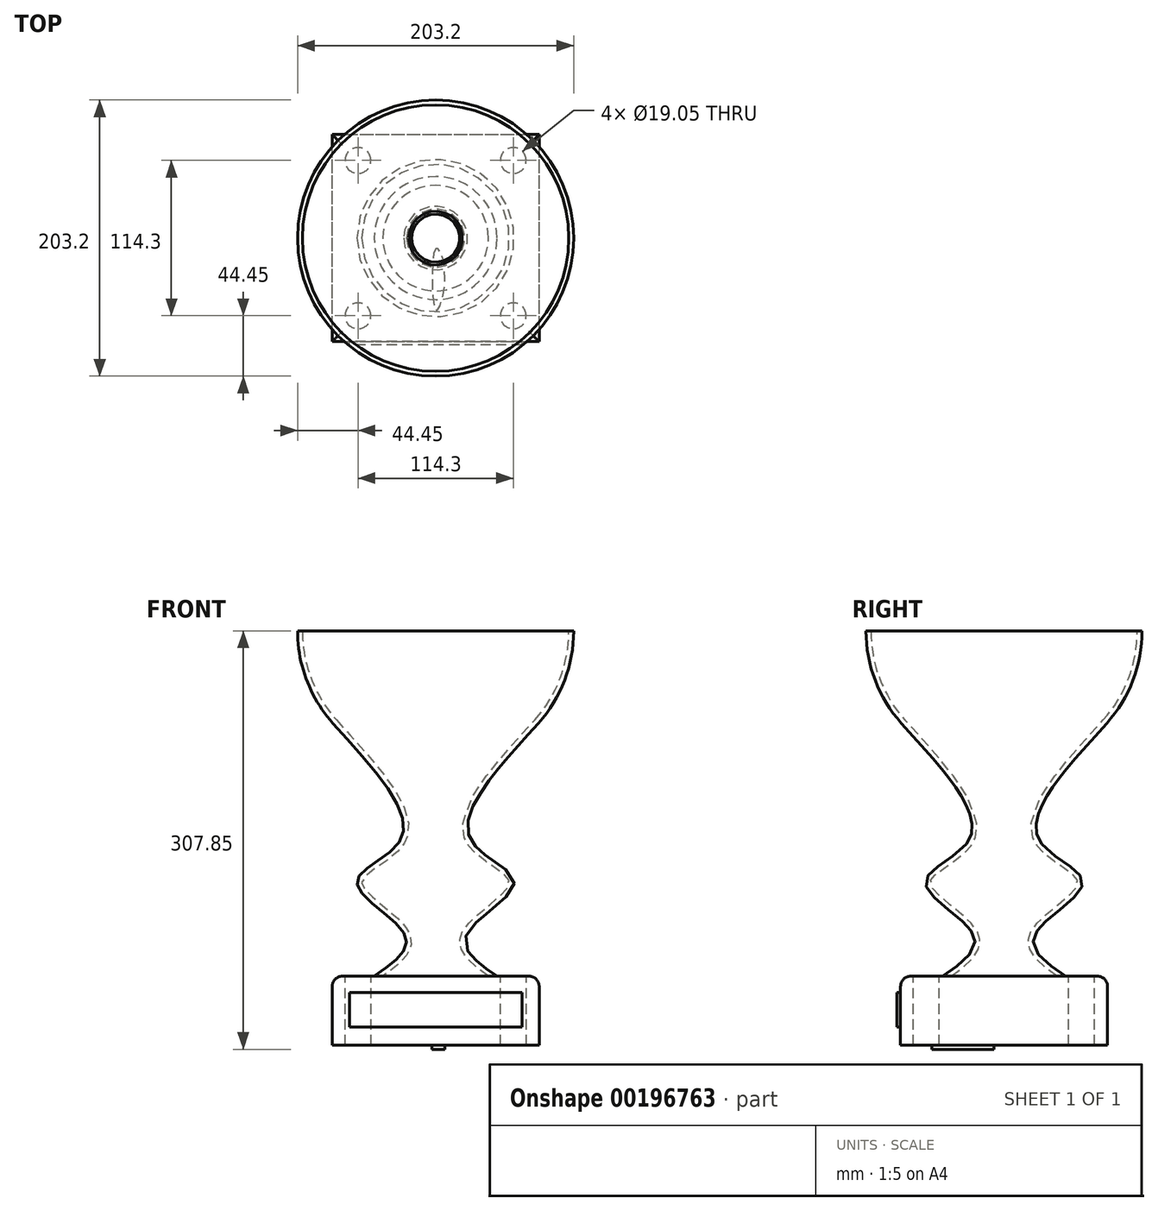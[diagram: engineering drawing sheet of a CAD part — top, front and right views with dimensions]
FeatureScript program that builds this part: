
annotation { "Feature Type Name" : "Feature", "Feature Type Description" : "" }
export const myFeature = defineFeature(function(context is Context, id is Id, definition is map)
    precondition{}
    {
        {
            var Q0;
            Q0=qCreatedBy(makeId("Top.planeOp"),FACE);
            var sketch = newSketch(context, id + "F0", { "sketchPlane" : qUnion([Q0])});
            skLineSegment(sketch, "E0.bottom", {"start": v(-76.2, -76.2) * mm, "end": v(76.2, -76.2) * mm});
            skLineSegment(sketch, "E0.top", {"start": v(-76.2, 76.2) * mm, "end": v(76.2, 76.2) * mm});
            skLineSegment(sketch, "E0.left", {"start": v(-76.2, -76.2) * mm, "end": v(-76.2, 76.2) * mm});
            skLineSegment(sketch, "E0.right", {"start": v(76.2, -76.2) * mm, "end": v(76.2, 76.2) * mm});
            skPoint(sketch, "E0.middle", {"position": v(0, 0) * mm});
            skSolve(sketch);
        }
        {
            var Q0;
            Q0=makeQuery(id+"F0.imprint","IMPRINT",FACE,{"disambiguationData":[TD([[makeQuery(id+"F0.imprint","IMPRINT",EDGE,{"derivedFrom":sQuery(id+"F0.wireOp",EDGE,"E0.bottom")}),1.0]])]});
            extrude(context, id + "F1", {"entities" : qUnion([Q0]), "depth" : 50.8 * mm});
        }
        {
            var Q0;
            Q0=makeQuery(id+"F1.opExtrude","SWEPT_FACE",FACE,{"disambiguationData":[OSD([sQuery(id+"F0.wireOp",EDGE,"E0.bottom")])]});
            var sketch = newSketch(context, id + "F2", { "sketchPlane" : qUnion([Q0])});
            skLineSegment(sketch, "E1.bottom", {"start": v(63.5, 38.64) * mm, "end": v(-63.5, 38.64) * mm});
            skLineSegment(sketch, "E1.top", {"start": v(63.5, 13.24) * mm, "end": v(-63.5, 13.24) * mm});
            skLineSegment(sketch, "E1.left", {"start": v(63.5, 38.64) * mm, "end": v(63.5, 13.24) * mm});
            skLineSegment(sketch, "E1.right", {"start": v(-63.5, 38.64) * mm, "end": v(-63.5, 13.24) * mm});
            skPoint(sketch, "E1.middle", {"position": v(0, 25.94) * mm});
            skPoint(sketch, "E1.middle.positionSnap0", {"position": v(0, 50.8) * mm});
            skPoint(sketch, "E1.centerSnap0", {"position": v(0, 50.8) * mm});
            skSolve(sketch);
        }
        {
            var Q0;
            Q0=makeQuery(id+"F2.imprint","IMPRINT",FACE,{"disambiguationData":[TD([[makeQuery(id+"F2.imprint","IMPRINT",EDGE,{"derivedFrom":sQuery(id+"F2.wireOp",EDGE,"E1.bottom")}),1.0]])]});
            extrude(context, id + "F3", {"entities" : qUnion([Q0]), "depth" : 2.54 * mm});
        }
        {
            var Q0;
            Q0=qCreatedBy(makeId("Front.planeOp"),FACE);
            var sketch = newSketch(context, id + "F4", { "sketchPlane" : qUnion([Q0])});
            skLineSegment(sketch, "E2", {"start": v(0, 50.8) * mm, "end": v(0, 304.8) * mm, "construction": true});
            skArc(sketch, "E3", {"start": v(75.66, 237) * mm, "mid": v(94.9, 268.5) * mm, "end": v(101.6, 304.8) * mm});
            skFitSpline(sketch, "E4", {"points": [v(75.66, 237) * mm, v(25.1, 152.4) * mm, v(57.89, 119.6) * mm, v(22.12, 80.1) * mm, v(45.97, 50.3) * mm], "startDerivative": vector(-245.19, -273.59) * mm, "endDerivative": vector(201.73, -135.91) * mm});
            skLineSegment(sketch, "E5", {"start": v(98.04, 304.8) * mm, "end": v(101.6, 304.8) * mm});
            skArc(sketch, "E6.0", {"start": v(73.01, 239.37) * mm, "mid": v(91.57, 269.77) * mm, "end": v(98.04, 304.8) * mm});
            skFitSpline(sketch, "E6.1", {"points": [v(73.01, 239.37) * mm, v(67.92, 233.68) * mm, v(59.91, 224.9) * mm, v(49.51, 213.07) * mm, v(42.1, 204.21) * mm, v(35.33, 195.44) * mm, v(29.43, 186.83) * mm, v(24.67, 178.44) * mm, v(21.86, 171.63) * mm, v(20.47, 166.3) * mm, v(19.9, 162.34) * mm, v(19.87, 158.45) * mm, v(20.36, 155.28) * mm, v(21.08, 152.81) * mm, v(21.67, 151.3) * mm, v(22.23, 150.14) * mm, v(22.84, 149) * mm, v(23.7, 147.62) * mm, v(24.83, 146.06) * mm, v(26.48, 144.07) * mm, v(28.76, 141.74) * mm, v(31.74, 139.16) * mm, v(35.92, 135.95) * mm, v(40.22, 133) * mm, v(44.27, 130.22) * mm, v(47.1, 128.21) * mm, v(49.58, 126.28) * mm, v(51.63, 124.44) * mm, v(53.14, 122.72) * mm, v(53.88, 121.49) * mm, v(54.2, 120.66) * mm, v(54.3, 120.2) * mm, v(54.33, 119.85) * mm, v(54.34, 119.6) * mm, v(54.32, 119.33) * mm, v(54.26, 118.93) * mm, v(54.1, 118.36) * mm, v(53.68, 117.29) * mm, v(52.76, 115.7) * mm, v(51.05, 113.54) * mm, v(48.84, 111.2) * mm, v(46.21, 108.75) * mm, v(42.31, 105.37) * mm, v(36.92, 101) * mm, v(31.46, 96.5) * mm, v(27.42, 92.84) * mm, v(24.62, 90.06) * mm, v(22.57, 87.69) * mm, v(21.13, 85.74) * mm, v(20.17, 84.24) * mm, v(19.48, 82.96) * mm, v(19, 81.9) * mm, v(18.58, 80.82) * mm, v(18.17, 79.46) * mm, v(17.79, 77.26) * mm, v(17.8, 74.52) * mm, v(18.53, 71.4) * mm, v(19.82, 68.48) * mm, v(21.56, 65.77) * mm, v(23.66, 63.2) * mm, v(26.86, 59.94) * mm, v(31.47, 56.07) * mm, v(37.62, 51.63) * mm, v(41.88, 48.77) * mm, v(43.98, 47.35) * mm]});
            skLineSegment(sketch, "E7.0", {"start": v(-76.2, 50.8) * mm, "end": v(76.2, 50.8) * mm});
            skSolve(sketch);
        }
        {
            var Q0;
            Q0=makeQuery(id+"F4.imprint","IMPRINT",FACE,{"disambiguationData":[TD([[makeQuery(id+"F4.imprint","IMPRINT",EDGE,{"derivedFrom":sQuery(id+"F4.wireOp",EDGE,"E3")}),1.0]])]});
            var Q1;
            Q1=sQuery(id+"F4.wireOp",EDGE,"E2");
            revolve(context, id + "F5", {"entities" : qUnion([Q0]), "axis" : qUnion([Q1]), "revolveType" : RevolveType.FULL});
        }
        {
            var Q0;
            Q0=makeQuery(id+"F1.opExtrude","CAP_FACE",FACE,{"disambiguationData":[OSD([sQuery(id+"F0.wireOp",EDGE,"E0.bottom"),sQuery(id+"F0.wireOp",EDGE,"E0.top"),sQuery(id+"F0.wireOp",EDGE,"E0.left"),sQuery(id+"F0.wireOp",EDGE,"E0.right")])],"isStart":false});
            var sketch = newSketch(context, id + "F6", { "sketchPlane" : qUnion([Q0])});
            skSolve(sketch);
        }
        {
            var Q0;
            Q0=makeQuery(id+"F6.imprint","IMPRINT",FACE,{"disambiguationData":[TD([[makeQuery(id+"F6.imprint","IMPRINT",EDGE,{"derivedFrom":makeQuery(id+"F1.opExtrude","CAP_EDGE",EDGE,{"disambiguationData":[OSD([sQuery(id+"F0.wireOp",EDGE,"E0.bottom")])],"isStart":false})}),1.0]])]});
            var sketch = newSketch(context, id + "F7", { "sketchPlane" : qUnion([Q0])});
            skCircle(sketch, "E8", {"center": v(-57.15, 57.15) * mm, "radius": 9.53 * mm});
            skCircle(sketch, "E9.0.1.0", {"center": v(-57.15, -57.15) * mm, "radius": 9.53 * mm});
            skCircle(sketch, "E9.1.0.0", {"center": v(57.15, 57.15) * mm, "radius": 9.53 * mm});
            skCircle(sketch, "E9.1.1.0", {"center": v(57.15, -57.15) * mm, "radius": 9.53 * mm});
            skLineSegment(sketch, "E9.direction1", {"start": v(-57.15, 57.15) * mm, "end": v(57.15, 57.15) * mm, "construction": true});
            skLineSegment(sketch, "E9.direction2", {"start": v(-57.15, 57.15) * mm, "end": v(-57.15, -57.15) * mm, "construction": true});
            skSolve(sketch);
        }
        {
            var Q0;
            Q0 = qSketchRegion(id + "F7", true);
            extrude(context, id + "F8", {"entities" : qUnion([Q0]), "operationType" : NewBodyOperationType.REMOVE, "oppositeDirection" : true, "depth" : 110.24 * mm});
        }
        {
            var Q0;
            Q0=makeQuery(id+"F1.opExtrude","CAP_EDGE",EDGE,{"disambiguationData":[OSD([sQuery(id+"F0.wireOp",EDGE,"E0.right")])],"isStart":false});
            var Q1;
            Q1=makeQuery(id+"F1.opExtrude","CAP_EDGE",EDGE,{"disambiguationData":[OSD([sQuery(id+"F0.wireOp",EDGE,"E0.bottom")])],"isStart":false});
            var Q2;
            Q2=makeQuery(id+"F1.opExtrude","CAP_EDGE",EDGE,{"disambiguationData":[OSD([sQuery(id+"F0.wireOp",EDGE,"E0.left")])],"isStart":false});
            var Q3;
            Q3=makeQuery(id+"F1.opExtrude","CAP_EDGE",EDGE,{"disambiguationData":[OSD([sQuery(id+"F0.wireOp",EDGE,"E0.top")])],"isStart":false});
            fillet(context, id + "F9", {"entities" : qUnion([Q0, Q1, Q2, Q3]), "radius" : 7.62 * mm, "tangentPropagation" : true, "allowEdgeOverflow" : false});
        }
        {
            var Q0;
            Q0=makeQuery(id+"F1.opExtrude","CAP_FACE",FACE,{"disambiguationData":[OSD([sQuery(id+"F0.wireOp",EDGE,"E0.bottom"),sQuery(id+"F0.wireOp",EDGE,"E0.top"),sQuery(id+"F0.wireOp",EDGE,"E0.left"),sQuery(id+"F0.wireOp",EDGE,"E0.right")])],"isStart":true});
            var sketch = newSketch(context, id + "F10", { "sketchPlane" : qUnion([Q0])});
            skFitSpline(sketch, "E10", {"points": [v(0, 7.7) * mm, v(0, 52.95) * mm, v(5.78, 40.86) * mm, v(6.55, 25.95) * mm, v(6.29, 20.3) * mm, v(4.75, 13.36) * mm, v(0, 7.7) * mm]});
            skSolve(sketch);
        }
        {
            var Q0;
            Q0=makeQuery(id+"F10.imprint","IMPRINT",FACE,{"disambiguationData":[TD([[makeQuery(id+"F10.imprint","IMPRINT",EDGE,{"derivedFrom":sQuery(id+"F10.wireOp",EDGE,"E10")}),-1.0]])]});
            extrude(context, id + "F11", {"entities" : qUnion([Q0]), "operationType" : NewBodyOperationType.ADD, "depth" : 3.05 * mm});
        }
    });
